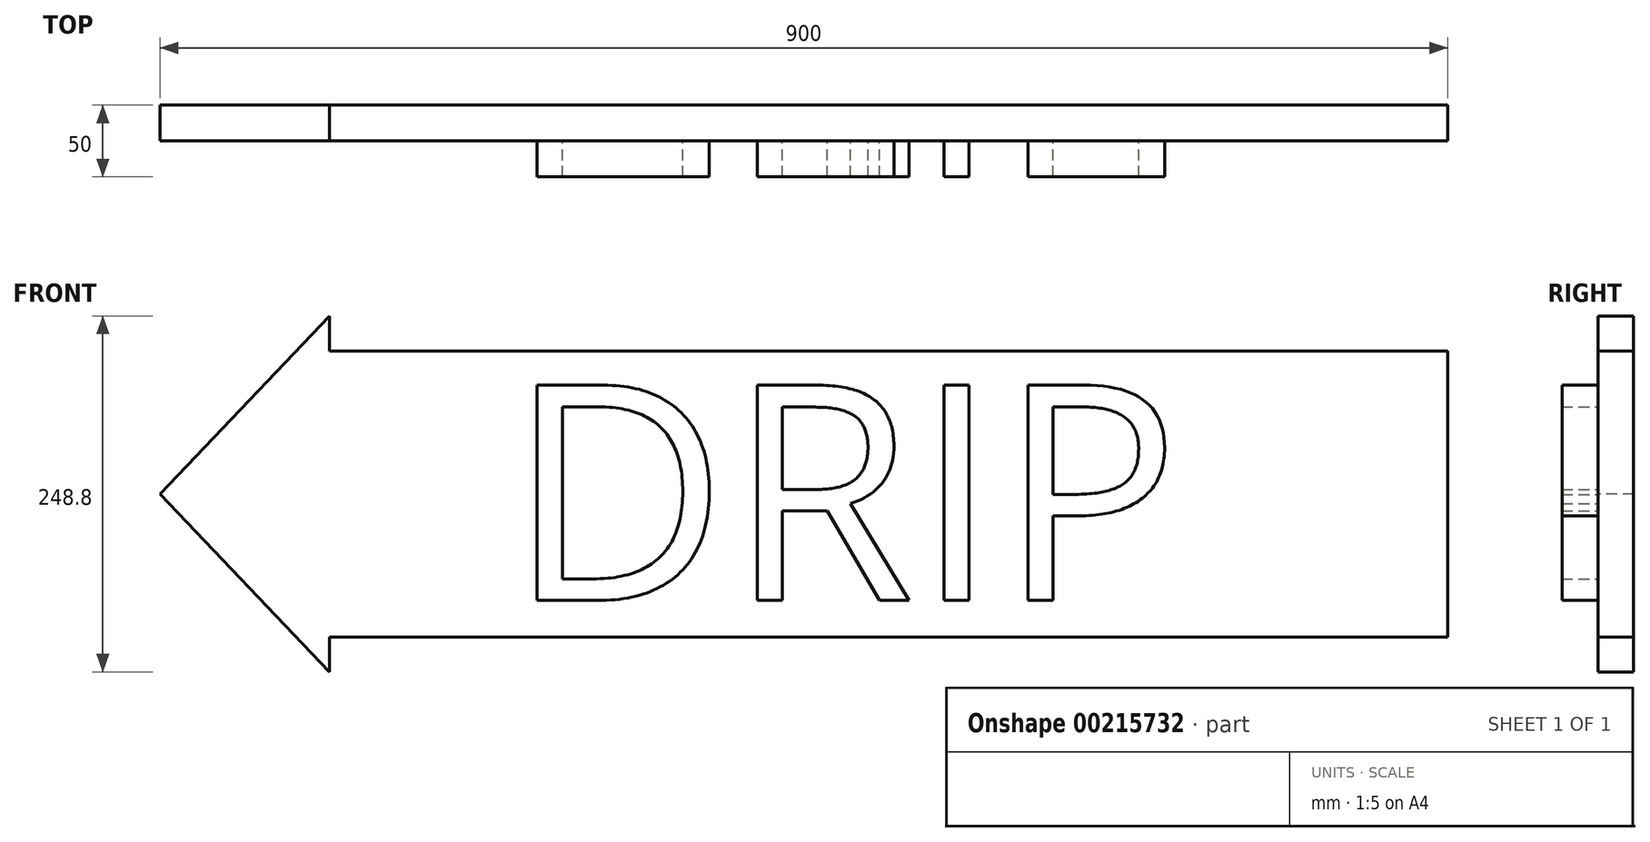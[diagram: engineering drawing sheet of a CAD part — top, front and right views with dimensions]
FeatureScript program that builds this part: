
annotation { "Feature Type Name" : "Feature", "Feature Type Description" : "" }
export const myFeature = defineFeature(function(context is Context, id is Id, definition is map)
    precondition{}
    {
        {
            var Q0;
            Q0=qCreatedBy(makeId("Front.planeOp"),FACE);
            var sketch = newSketch(context, id + "F0", { "sketchPlane" : qUnion([Q0])});
            skLineSegment(sketch, "E0", {"start": v(0, 0) * mm, "end": v(0, 100) * mm});
            skLineSegment(sketch, "E1.MirrorCS", {"start": v(0, 0) * mm, "end": v(0, -100) * mm});
            skLineSegment(sketch, "E2.MirrorCS", {"start": v(-781.62, 100) * mm, "end": v(-781.62, 124.4) * mm});
            skLineSegment(sketch, "E3.MirrorCS", {"start": v(-781.62, -100) * mm, "end": v(-781.62, -124.4) * mm});
            skLineSegment(sketch, "E4.MirrorCS", {"start": v(-781.62, 124.4) * mm, "end": v(-900, 0) * mm});
            skLineSegment(sketch, "E5.MirrorCS", {"start": v(0, 100) * mm, "end": v(-781.62, 100) * mm});
            skLineSegment(sketch, "E6.MirrorCS", {"start": v(0, -100) * mm, "end": v(-781.62, -100) * mm});
            skLineSegment(sketch, "E7.MirrorCS", {"start": v(-781.62, -124.4) * mm, "end": v(-900, 0) * mm});
            skLineSegment(sketch, "E8.MirrorCS", {"start": v(-900, 0) * mm, "end": v(0, 0) * mm});
            skSolve(sketch);
        }
        {
            var Q0;
            Q0=qSketchRegion(id+"F0",true);
            extrude(context, id + "F1", {"entities" : qUnion([Q0]), "oppositeDirection" : true, "depth" : 25 * mm});
        }
        {
            var Q0;
            Q0=qCreatedBy(makeId("Front.planeOp"),FACE);
            var sketch = newSketch(context, id + "F2", { "sketchPlane" : qUnion([Q0])});
            skText(sketch, "E9", { "text": "DRIP", "fontName": "OpenSans-Regular.ttf"});
            const initialGuessF2  = {"E9": [-0.6571, -0.07451, 1, 0, 0.15191]};
            skSetInitialGuess(sketch, initialGuessF2);
            skSolve(sketch);
        }
        {
            var Q0;
            Q0 = qSketchRegion(id + "F2", true);
            extrude(context, id + "F3", {"entities" : qUnion([Q0]), "operationType" : NewBodyOperationType.ADD, "depth" : 25 * mm});
        }
    });
